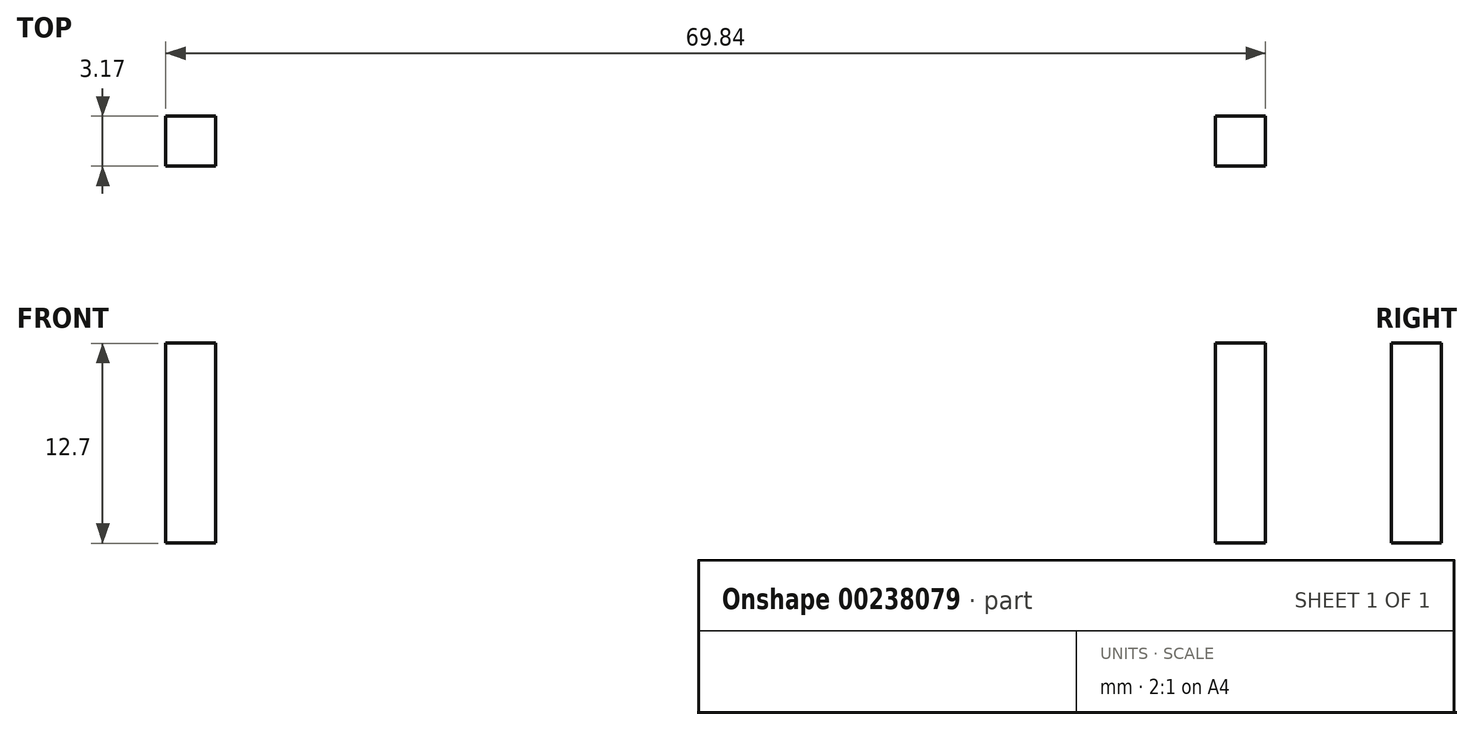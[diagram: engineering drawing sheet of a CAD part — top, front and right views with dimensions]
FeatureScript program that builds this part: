
annotation { "Feature Type Name" : "Feature", "Feature Type Description" : "" }
export const myFeature = defineFeature(function(context is Context, id is Id, definition is map)
    precondition{}
    {
        {
            var Q0;
            Q0=qCreatedBy(makeId("Front.planeOp"),FACE);
            var sketch = newSketch(context, id + "F0", { "sketchPlane" : qUnion([Q0])});
            skLineSegment(sketch, "E0.bottom", {"start": v(-31.75, 30.16) * mm, "end": v(31.75, 30.16) * mm});
            skLineSegment(sketch, "E0.top", {"start": v(-31.75, -30.16) * mm, "end": v(31.75, -30.16) * mm});
            skLineSegment(sketch, "E0.left", {"start": v(-31.75, 30.16) * mm, "end": v(-31.75, -30.16) * mm});
            skLineSegment(sketch, "E0.right", {"start": v(31.75, 30.16) * mm, "end": v(31.75, -30.16) * mm});
            skPoint(sketch, "E0.middle", {"position": v(0, 0) * mm});
            skLineSegment(sketch, "E1.bottom", {"start": v(-6.35, -30.16) * mm, "end": v(6.35, -30.16) * mm});
            skLineSegment(sketch, "E1.top", {"start": v(-6.35, -33.34) * mm, "end": v(6.35, -33.34) * mm});
            skLineSegment(sketch, "E1.left", {"start": v(-6.35, -30.16) * mm, "end": v(-6.35, -33.34) * mm});
            skLineSegment(sketch, "E1.right", {"start": v(6.35, -30.16) * mm, "end": v(6.35, -33.34) * mm});
            skLineSegment(sketch, "E2.bottom", {"start": v(-34.93, 3.18) * mm, "end": v(-31.75, 3.18) * mm});
            skLineSegment(sketch, "E2.top", {"start": v(-34.93, -9.52) * mm, "end": v(-31.75, -9.52) * mm});
            skLineSegment(sketch, "E2.left", {"start": v(-34.93, 3.18) * mm, "end": v(-34.93, -9.52) * mm});
            skLineSegment(sketch, "E2.right", {"start": v(-31.75, 3.18) * mm, "end": v(-31.75, -9.53) * mm});
            skLineSegment(sketch, "E3.bottom", {"start": v(31.75, 3.18) * mm, "end": v(34.93, 3.18) * mm});
            skLineSegment(sketch, "E3.top", {"start": v(31.75, -9.52) * mm, "end": v(34.93, -9.52) * mm});
            skLineSegment(sketch, "E3.left", {"start": v(31.75, 3.18) * mm, "end": v(31.75, -9.52) * mm});
            skLineSegment(sketch, "E3.right", {"start": v(34.93, 3.18) * mm, "end": v(34.93, -9.52) * mm});
            skLineSegment(sketch, "E4.bottom", {"start": v(-20.32, 30.16) * mm, "end": v(-13.97, 30.16) * mm});
            skLineSegment(sketch, "E4.top", {"start": v(-20.32, 23.81) * mm, "end": v(-13.97, 23.81) * mm});
            skLineSegment(sketch, "E4.left", {"start": v(-20.32, 30.16) * mm, "end": v(-20.32, 23.81) * mm});
            skLineSegment(sketch, "E4.right", {"start": v(-13.97, 30.16) * mm, "end": v(-13.97, 23.81) * mm});
            skLineSegment(sketch, "E5.0", {"start": v(-2.54, 30.16) * mm, "end": v(-5.72, 20.64) * mm});
            skLineSegment(sketch, "E5.1", {"start": v(-5.72, 20.64) * mm, "end": v(-8.89, 30.16) * mm});
            skLineSegment(sketch, "E5.2", {"start": v(-8.89, 30.16) * mm, "end": v(-2.54, 30.16) * mm});
            skLineSegment(sketch, "E6.0", {"start": v(17.15, 30.16) * mm, "end": v(15.56, 20.64) * mm});
            skLineSegment(sketch, "E6.1", {"start": v(15.56, 20.64) * mm, "end": v(13.97, 30.16) * mm});
            skLineSegment(sketch, "E6.2", {"start": v(13.97, 30.16) * mm, "end": v(17.15, 30.16) * mm});
            skLineSegment(sketch, "E7.0", {"start": v(20.32, 30.16) * mm, "end": v(18.73, 20.64) * mm});
            skLineSegment(sketch, "E7.1", {"start": v(18.73, 20.64) * mm, "end": v(17.15, 30.16) * mm});
            skLineSegment(sketch, "E7.2", {"start": v(17.15, 30.16) * mm, "end": v(20.32, 30.16) * mm});
            skSolve(sketch);
        }
        {
            var Q0;
            {var subQ10=sQuery(id+"F0.wireOp",EDGE,"E1.bottom");Q0=makeQuery(id+"F0.imprint","IMPRINT",FACE,{"disambiguationData":[TD([[makeQuery(id+"F0.imprint","IMPRINT",EDGE,{"derivedFrom":subQ10}),1.0]])]});}
            var Q1;
            Q1=makeQuery(id+"F0.imprint","IMPRINT",FACE,{"disambiguationData":[TD([[makeQuery(id+"F0.imprint","IMPRINT",EDGE,{"derivedFrom":sQuery(id+"F0.wireOp",EDGE,"E3.bottom")}),-1.0]])]});
            var Q2;
            Q2=makeQuery(id+"F0.imprint","IMPRINT",FACE,{"disambiguationData":[TD([[makeQuery(id+"F0.imprint","IMPRINT",EDGE,{"derivedFrom":sQuery(id+"F0.wireOp",EDGE,"E1.bottom")}),-1.0]])]});
            var Q3;
            Q3=makeQuery(id+"F0.imprint","IMPRINT",FACE,{"disambiguationData":[TD([[makeQuery(id+"F0.imprint","IMPRINT",EDGE,{"derivedFrom":sQuery(id+"F0.wireOp",EDGE,"E2.bottom")}),-1.0]])]});
            extrude(context, id + "F1", {"entities" : qUnion([Q0, Q1, Q2, Q3]), "depth" : 3.17 * mm});
        }
    });
